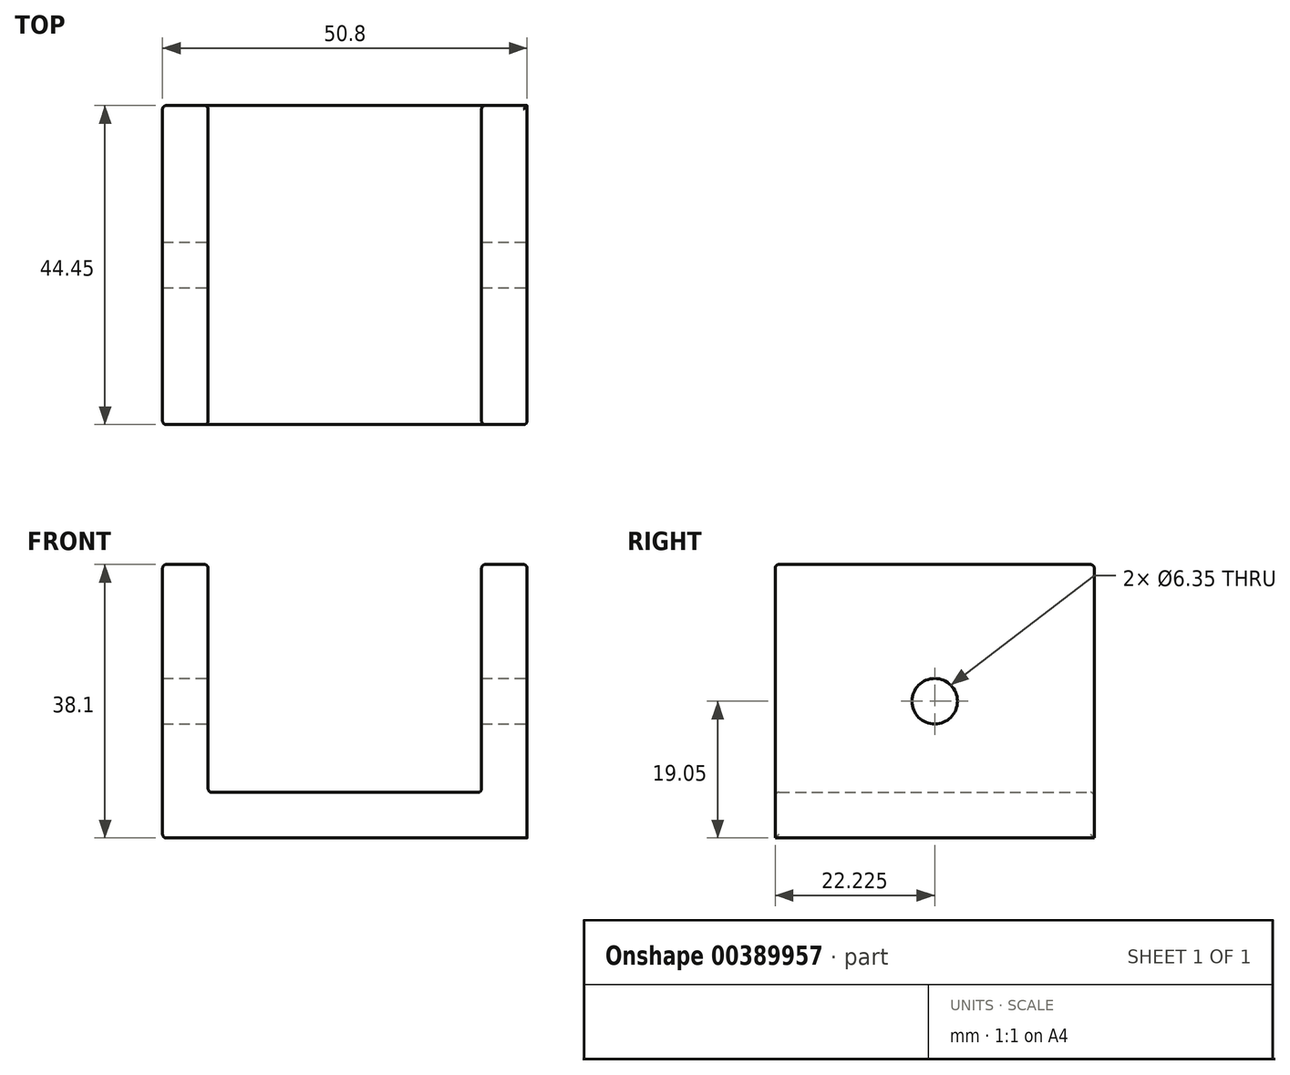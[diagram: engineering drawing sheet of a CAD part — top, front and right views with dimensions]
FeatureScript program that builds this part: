
annotation { "Feature Type Name" : "Feature", "Feature Type Description" : "" }
export const myFeature = defineFeature(function(context is Context, id is Id, definition is map)
    precondition{}
    {
        {
            var Q0;
            Q0=qCreatedBy(makeId("Front.planeOp"),FACE);
            var sketch = newSketch(context, id + "F0", { "sketchPlane" : qUnion([Q0])});
            skLineSegment(sketch, "E0", {"start": v(0, 0) * mm, "end": v(19.05, 0) * mm});
            skLineSegment(sketch, "E1", {"start": v(19.05, 0) * mm, "end": v(19.05, 31.75) * mm});
            skLineSegment(sketch, "E2.0", {"start": v(25.4, -6.35) * mm, "end": v(25.4, 31.75) * mm});
            skLineSegment(sketch, "E2.1", {"start": v(-26.33, -6.35) * mm, "end": v(25.4, -6.35) * mm});
            skLineSegment(sketch, "E3", {"start": v(19.05, 31.75) * mm, "end": v(25.4, 31.75) * mm});
            skLineSegment(sketch, "E4.MirrorCS", {"start": v(0, 0) * mm, "end": v(-19.05, 0) * mm});
            skLineSegment(sketch, "E5.MirrorCS", {"start": v(26.33, -6.35) * mm, "end": v(-25.4, -6.35) * mm});
            skLineSegment(sketch, "E6.MirrorCS", {"start": v(-25.4, -6.35) * mm, "end": v(-25.4, 31.75) * mm});
            skLineSegment(sketch, "E7.MirrorCS", {"start": v(-19.05, 0) * mm, "end": v(-19.05, 31.75) * mm});
            skLineSegment(sketch, "E8.MirrorCS", {"start": v(-19.05, 31.75) * mm, "end": v(-25.4, 31.75) * mm});
            skSolve(sketch);
        }
        {
            var Q0;
            Q0=makeQuery(id+"F0.imprint","IMPRINT",FACE,{"disambiguationData":[TD([[makeQuery(id+"F0.imprint","IMPRINT",EDGE,{"derivedFrom":sQuery(id+"F0.wireOp",EDGE,"E0")}),-1.0]])]});
            extrude(context, id + "F1", {"entities" : qUnion([Q0]), "depth" : 44.45 * mm});
        }
        {
            var Q0;
            Q0=makeQuery(id+"F1.opExtrude","SWEPT_FACE",FACE,{"disambiguationData":[OSD([sQuery(id+"F0.wireOp",EDGE,"E2.0")])]});
            var sketch = newSketch(context, id + "F2", { "sketchPlane" : qUnion([Q0])});
            skLineSegment(sketch, "E9", {"start": v(-44.45, 12.7) * mm, "end": v(0, 12.7) * mm, "construction": true});
            skCircle(sketch, "E10", {"center": v(-22.23, 12.7) * mm, "radius": 3.18 * mm});
            skSolve(sketch);
        }
        {
            var Q0;
            Q0=sQuery(id+"F2.wireOp",VERTEX,"E10.center");
            var Q1;
            Q1=makeQuery(id+"F1.opExtrude","SWEPT_BODY",BODY,{"disambiguationData":[OSD([sQuery(id+"F0.wireOp",EDGE,"E0"),sQuery(id+"F0.wireOp",EDGE,"E1"),sQuery(id+"F0.wireOp",EDGE,"E2.0"),sQuery(id+"F0.wireOp",EDGE,"E3"),sQuery(id+"F0.wireOp",EDGE,"E4.MirrorCS"),sQuery(id+"F0.wireOp",EDGE,"E5.MirrorCS"),sQuery(id+"F0.wireOp",EDGE,"E6.MirrorCS"),sQuery(id+"F0.wireOp",EDGE,"E7.MirrorCS"),sQuery(id+"F0.wireOp",EDGE,"E8.MirrorCS")])]});
            hole(context, id + "F3", {"style" : HoleStyle.SIMPLE, "endStyle" : HoleEndStyle.THROUGH, "holeDiameter" : 6.35 * mm, "isTappedThrough" : true, "tappedDepth" : 12.7 * mm, "tapClearance" : 3, "locations" : qUnion([Q0]), "scope" : qUnion([Q1])});
        }
        {
            var Q0;
            Q0=makeQuery(id+"F1.opExtrude","SWEPT_EDGE",EDGE,{"disambiguationData":[OSD([sQuery(id+"F0.wireOp",EDGE,"E7.MirrorCS"),sQuery(id+"F0.wireOp",EDGE,"E8.MirrorCS")])]});
            var Q1;
            Q1=makeQuery(id+"F1.opExtrude","SWEPT_EDGE",EDGE,{"disambiguationData":[OSD([sQuery(id+"F0.wireOp",EDGE,"E1"),sQuery(id+"F0.wireOp",EDGE,"E3")])]});
            var Q2;
            Q2=makeQuery(id+"F1.opExtrude","SWEPT_EDGE",EDGE,{"disambiguationData":[OSD([sQuery(id+"F0.wireOp",EDGE,"E2.0"),sQuery(id+"F0.wireOp",EDGE,"E3")])]});
            var Q3;
            Q3=makeQuery(id+"F1.opExtrude","CAP_EDGE",EDGE,{"disambiguationData":[OSD([sQuery(id+"F0.wireOp",EDGE,"E3")])],"isStart":false});
            var Q4;
            Q4=makeQuery(id+"F1.opExtrude","CAP_EDGE",EDGE,{"disambiguationData":[OSD([sQuery(id+"F0.wireOp",EDGE,"E3")])],"isStart":true});
            var Q5;
            Q5=makeQuery(id+"F1.opExtrude","CAP_EDGE",EDGE,{"disambiguationData":[OSD([sQuery(id+"F0.wireOp",EDGE,"E2.0")])],"isStart":false});
            var Q6;
            Q6=makeQuery(id+"F1.opExtrude","CAP_EDGE",EDGE,{"disambiguationData":[OSD([sQuery(id+"F0.wireOp",EDGE,"E1")])],"isStart":false});
            var Q7;
            Q7=makeQuery(id+"F1.opExtrude","CAP_EDGE",EDGE,{"disambiguationData":[OSD([sQuery(id+"F0.wireOp",EDGE,"E0"),sQuery(id+"F0.wireOp",EDGE,"E4.MirrorCS")])],"isStart":false});
            var Q8;
            Q8=makeQuery(id+"F1.opExtrude","SWEPT_FACE",FACE,{"disambiguationData":[OSD([sQuery(id+"F0.wireOp",EDGE,"E0"),sQuery(id+"F0.wireOp",EDGE,"E4.MirrorCS")])]});
            var Q9;
            Q9=makeQuery(id+"F1.opExtrude","CAP_EDGE",EDGE,{"disambiguationData":[OSD([sQuery(id+"F0.wireOp",EDGE,"E7.MirrorCS")])],"isStart":false});
            var Q10;
            Q10=makeQuery(id+"F1.opExtrude","CAP_EDGE",EDGE,{"disambiguationData":[OSD([sQuery(id+"F0.wireOp",EDGE,"E7.MirrorCS")])],"isStart":true});
            var Q11;
            Q11=makeQuery(id+"F1.opExtrude","SWEPT_EDGE",EDGE,{"disambiguationData":[OSD([sQuery(id+"F0.wireOp",EDGE,"E6.MirrorCS"),sQuery(id+"F0.wireOp",EDGE,"E8.MirrorCS")])]});
            var Q12;
            Q12=makeQuery(id+"F1.opExtrude","CAP_EDGE",EDGE,{"disambiguationData":[OSD([sQuery(id+"F0.wireOp",EDGE,"E8.MirrorCS")])],"isStart":true});
            var Q13;
            Q13=makeQuery(id+"F1.opExtrude","CAP_EDGE",EDGE,{"disambiguationData":[OSD([sQuery(id+"F0.wireOp",EDGE,"E8.MirrorCS")])],"isStart":false});
            var Q14;
            Q14=makeQuery(id+"F1.opExtrude","CAP_EDGE",EDGE,{"disambiguationData":[OSD([sQuery(id+"F0.wireOp",EDGE,"E6.MirrorCS")])],"isStart":false});
            var Q15;
            Q15=makeQuery(id+"F1.opExtrude","CAP_EDGE",EDGE,{"disambiguationData":[OSD([sQuery(id+"F0.wireOp",EDGE,"E5.MirrorCS")])],"isStart":false});
            var Q16;
            Q16=makeQuery(id+"F1.opExtrude","CAP_EDGE",EDGE,{"disambiguationData":[OSD([sQuery(id+"F0.wireOp",EDGE,"E5.MirrorCS")])],"isStart":true});
            var Q17;
            Q17=makeQuery(id+"F1.opExtrude","CAP_EDGE",EDGE,{"disambiguationData":[OSD([sQuery(id+"F0.wireOp",EDGE,"E6.MirrorCS")])],"isStart":true});
            var Q18;
            Q18=makeQuery(id+"F1.opExtrude","CAP_EDGE",EDGE,{"disambiguationData":[OSD([sQuery(id+"F0.wireOp",EDGE,"E1")])],"isStart":true});
            var Q19;
            Q19=makeQuery(id+"F1.opExtrude","SWEPT_EDGE",EDGE,{"disambiguationData":[OSD([sQuery(id+"F0.wireOp",EDGE,"E5.MirrorCS"),sQuery(id+"F0.wireOp",EDGE,"E6.MirrorCS")])]});
            fillet(context, id + "F4", {"entities" : qUnion([Q0, Q1, Q2, Q3, Q4, Q5, Q6, Q7, Q8, Q9, Q10, Q11, Q12, Q13, Q14, Q15, Q16, Q17, Q18, Q19]), "radius" : 0.5 * mm, "tangentPropagation" : true, "allowEdgeOverflow" : false});
        }
    });
